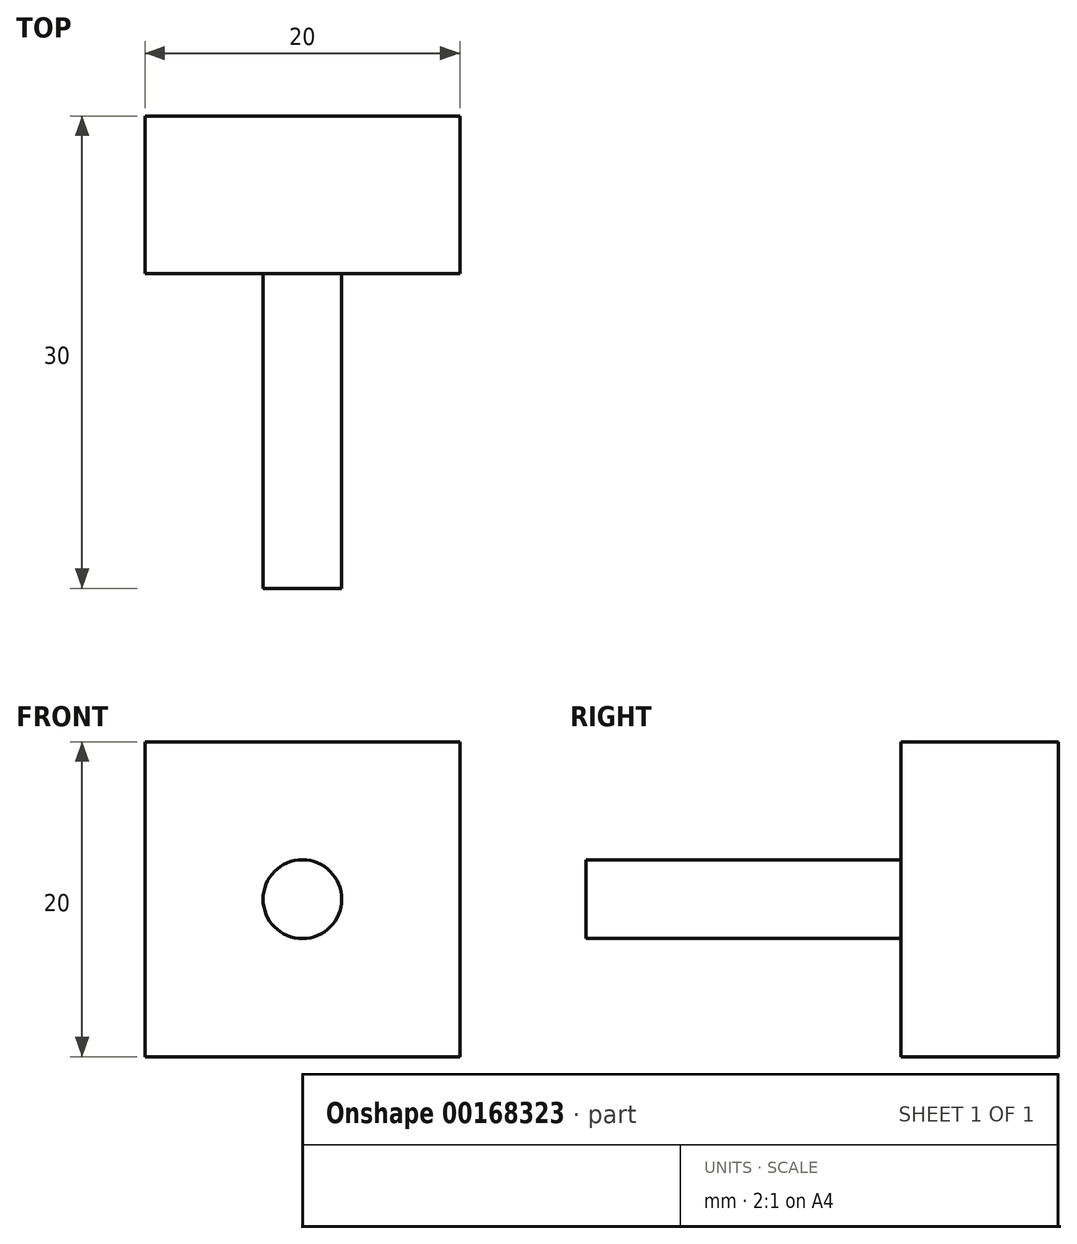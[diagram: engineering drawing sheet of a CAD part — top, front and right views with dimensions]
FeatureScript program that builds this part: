
annotation { "Feature Type Name" : "Feature", "Feature Type Description" : "" }
export const myFeature = defineFeature(function(context is Context, id is Id, definition is map)
    precondition{}
    {
        {
            var Q0;
            Q0=qCreatedBy(makeId("Top.planeOp"),FACE);
            var sketch = newSketch(context, id + "F0", { "sketchPlane" : qUnion([Q0])});
            skLineSegment(sketch, "E0.bottom", {"start": v(-10, 25) * mm, "end": v(10, 25) * mm});
            skLineSegment(sketch, "E0.top", {"start": v(-10, -25) * mm, "end": v(10, -25) * mm});
            skLineSegment(sketch, "E0.left", {"start": v(-10, 25) * mm, "end": v(-10, -25) * mm});
            skLineSegment(sketch, "E0.right", {"start": v(10, 25) * mm, "end": v(10, -25) * mm});
            skPoint(sketch, "E0.middle", {"position": v(0, 0) * mm});
            skSolve(sketch);
        }
        {
            var Q0;
            Q0=makeQuery(id+"F0.imprint","IMPRINT",FACE,{"disambiguationData":[TD([[makeQuery(id+"F0.imprint","IMPRINT",EDGE,{"derivedFrom":sQuery(id+"F0.wireOp",EDGE,"E0.bottom")}),-1.0]])]});
            extrude(context, id + "F1", {"entities" : qUnion([Q0]), "depth" : 60 * mm});
        }
        {
            var Q0;
            Q0=makeQuery(id+"F1.opExtrude","SWEPT_FACE",FACE,{"disambiguationData":[OSD([sQuery(id+"F0.wireOp",EDGE,"E0.top")])]});
            var sketch = newSketch(context, id + "F2", { "sketchPlane" : qUnion([Q0])});
            skCircle(sketch, "E1", {"center": v(0, 50) * mm, "radius": 2.5 * mm});
            skPoint(sketch, "E1.centerSnap0", {"position": v(0, 60) * mm});
            skSolve(sketch);
        }
        {
            var Q0;
            Q0=makeQuery(id+"F2.imprint","IMPRINT",FACE,{"disambiguationData":[TD([[makeQuery(id+"F2.imprint","IMPRINT",EDGE,{"derivedFrom":sQuery(id+"F2.wireOp",EDGE,"E1")}),1.0]])]});
            var Q1;
            Q1=makeQuery(id+"F2.imprint","IMPRINT",FACE,{"disambiguationData":[TD([[makeQuery(id+"F2.imprint","IMPRINT",EDGE,{"derivedFrom":sQuery(id+"F2.wireOp",EDGE,"anuL5Iv7-uxPJ-X4tW-e8Mz-K0PABbkokloh")}),1.0]])]});
            extrude(context, id + "F3", {"entities" : qUnion([Q0, Q1]), "operationType" : NewBodyOperationType.REMOVE, "oppositeDirection" : true, "depth" : 20 * mm});
        }
        {
            var Q0;
            Q0=makeQuery(id+"F1.opExtrude","CAP_FACE",FACE,{"disambiguationData":[OSD([sQuery(id+"F0.wireOp",EDGE,"E0.bottom"),sQuery(id+"F0.wireOp",EDGE,"E0.top"),sQuery(id+"F0.wireOp",EDGE,"E0.left"),sQuery(id+"F0.wireOp",EDGE,"E0.right")])],"isStart":true});
            extrude(context, id + "F4", {"entities" : qUnion([Q0]), "operationType" : NewBodyOperationType.ADD, "oppositeDirection" : true, "depth" : 40 * mm});
        }
        {
            var Q0;
            Q0=makeQuery(id+"F1.opExtrude","CAP_FACE",FACE,{"disambiguationData":[OSD([sQuery(id+"F0.wireOp",EDGE,"E0.bottom"),sQuery(id+"F0.wireOp",EDGE,"E0.top"),sQuery(id+"F0.wireOp",EDGE,"E0.left"),sQuery(id+"F0.wireOp",EDGE,"E0.right")])],"isStart":true});
            extrude(context, id + "F5", {"entities" : qUnion([Q0]), "operationType" : NewBodyOperationType.REMOVE, "oppositeDirection" : true, "depth" : 40 * mm});
        }
        {
            var Q0;
            Q0=makeQuery(id+"F1.opExtrude","SWEPT_FACE",FACE,{"disambiguationData":[OSD([sQuery(id+"F0.wireOp",EDGE,"E0.bottom")])]});
            extrude(context, id + "F6", {"entities" : qUnion([Q0]), "operationType" : NewBodyOperationType.REMOVE, "oppositeDirection" : true, "depth" : 25 * mm});
        }
        {
            var Q0;
            Q0=makeQuery(id+"F3.boolean.opBoolean","COPY",FACE,{"derivedFrom":makeQuery(id+"F3.opExtrude","CAP_FACE",FACE,{"disambiguationData":[OSD([sQuery(id+"F2.wireOp",EDGE,"E1")])],"isStart":false})});
            extrude(context, id + "F7", {"entities" : qUnion([Q0]), "operationType" : NewBodyOperationType.ADD, "depth" : 40 * mm});
        }
        {
            var Q0;
            Q0=makeQuery(id+"F6.boolean.opBoolean","COPY",FACE,{"derivedFrom":makeQuery(id+"F6.opExtrude","CAP_FACE",FACE,{"disambiguationData":[OSD([sQuery(id+"F0.wireOp",EDGE,"E0.bottom")])],"isStart":false})});
            extrude(context, id + "F8", {"entities" : qUnion([Q0]), "operationType" : NewBodyOperationType.REMOVE, "oppositeDirection" : true, "depth" : 15 * mm});
        }
    });
